FCSTD DOCUMENT  (FreeCAD 0.21R32532 (Git))
Label: 0
License: All rights reserved
LicenseURL: http://en.wikipedia.org/wiki/All_rights_reserved
objects: Part::Feature×1, Part::FeaturePython×1, Sketcher::SketchObject×1, PartDesign::SubShapeBinder×1
note: 4 computed .brp shape members not serialized (recipe doc carries the construction recipe); baked Part::Feature solids carry a one-line shape summary decoded from their .brp

FEATURE [Part::Feature] UNFOLD_SKETCH001
  shape: bbox 42770 x 1905 x 2e-07 mm, 0 faces, 0 solids (baked)
FEATURE [Part::FeaturePython] Clone  label="UNFOLD_SKETCH002"  # Draft clone (typed FeaturePython)
  AttacherType = Attacher::AttachEngine3D
  Fuse = false
  Objects = -> [UNFOLD_SKETCH001]
  Scale = (0.0393701,0.0393701,0.0393701)
  expr: .Scale.x = 1 / 25.4
  expr: .Scale.y = 1 / 25.4
  expr: .Scale.z = 1 / 25.4
FEATURE [Sketcher::SketchObject] Sketch
  FullyConstrained = true
  sketch-geometry (39):
    g0: Circle CenterX=1673 CenterY=0 CenterZ=0 NormalX=0 NormalY=0 NormalZ=1 AngleXU=0 Radius=1.7
    g1: Circle CenterX=1605 CenterY=-12.5 CenterZ=0 NormalX=0 NormalY=0 NormalZ=1 AngleXU=0 Radius=1.7
    g2: Circle CenterX=1605 CenterY=12.5 CenterZ=0 NormalX=0 NormalY=0 NormalZ=1 AngleXU=0 Radius=1.7
    g3: Circle CenterX=1584 CenterY=26.6981 CenterZ=0 NormalX=0 NormalY=0 NormalZ=1 AngleXU=0 Radius=1.7
    g4: Circle CenterX=1584 CenterY=0 CenterZ=0 NormalX=0 NormalY=0 NormalZ=1 AngleXU=0 Radius=1.7
    g5: Circle CenterX=1584 CenterY=-26.6981 CenterZ=0 NormalX=0 NormalY=0 NormalZ=1 AngleXU=0 Radius=1.7
    g6: Circle CenterX=1310.75 CenterY=-26.6981 CenterZ=0 NormalX=0 NormalY=0 NormalZ=1 AngleXU=0 Radius=1.7
    g7: Circle CenterX=1310.75 CenterY=0 CenterZ=0 NormalX=0 NormalY=0 NormalZ=1 AngleXU=0 Radius=1.7
    g8: Circle CenterX=1310.75 CenterY=26.6981 CenterZ=0 NormalX=0 NormalY=0 NormalZ=1 AngleXU=0 Radius=1.7
    g9: Circle CenterX=1037.5 CenterY=-26.6981 CenterZ=0 NormalX=0 NormalY=0 NormalZ=1 AngleXU=0 Radius=1.7
    g10: Circle CenterX=1037.5 CenterY=0 CenterZ=0 NormalX=0 NormalY=0 NormalZ=1 AngleXU=0 Radius=1.7
    g11: Circle CenterX=1037.5 CenterY=26.6981 CenterZ=0 NormalX=0 NormalY=0 NormalZ=1 AngleXU=0 Radius=1.7
    g12: Circle CenterX=764.248 CenterY=26.6981 CenterZ=0 NormalX=0 NormalY=0 NormalZ=1 AngleXU=0 Radius=1.7
    g13: Circle CenterX=764.248 CenterY=0 CenterZ=0 NormalX=0 NormalY=0 NormalZ=1 AngleXU=0 Radius=1.7
    g14: Circle CenterX=764.248 CenterY=-26.6981 CenterZ=0 NormalX=0 NormalY=0 NormalZ=1 AngleXU=0 Radius=1.7
    g15: Circle CenterX=490.999 CenterY=-26.6981 CenterZ=0 NormalX=0 NormalY=0 NormalZ=1 AngleXU=0 Radius=1.7
    g16: Circle CenterX=490.999 CenterY=0 CenterZ=0 NormalX=0 NormalY=0 NormalZ=1 AngleXU=0 Radius=1.7
    g17: Circle CenterX=469.999 CenterY=0 CenterZ=0 NormalX=0 NormalY=0 NormalZ=1 AngleXU=0 Radius=1.7
    g18: Circle CenterX=490.999 CenterY=26.6981 CenterZ=0 NormalX=0 NormalY=0 NormalZ=1 AngleXU=0 Radius=1.7
    g19: Circle CenterX=99.9998 CenterY=-26.1981 CenterZ=0 NormalX=0 NormalY=0 NormalZ=1 AngleXU=0 Radius=1.7
    g20: Circle CenterX=99.9998 CenterY=26.1981 CenterZ=0 NormalX=0 NormalY=0 NormalZ=1 AngleXU=0 Radius=1.7
    g21: Circle CenterX=71.3332 CenterY=26.1981 CenterZ=0 NormalX=0 NormalY=0 NormalZ=1 AngleXU=0 Radius=1.7
    g22: Circle CenterX=42.6666 CenterY=26.1981 CenterZ=0 NormalX=0 NormalY=0 NormalZ=1 AngleXU=0 Radius=1.7
    g23: Circle CenterX=14 CenterY=26.1981 CenterZ=0 NormalX=0 NormalY=0 NormalZ=1 AngleXU=0 Radius=1.7
    g24: Circle CenterX=14 CenterY=-26.1981 CenterZ=0 NormalX=0 NormalY=0 NormalZ=1 AngleXU=0 Radius=1.7
    g25: Circle CenterX=42.6666 CenterY=-26.1981 CenterZ=0 NormalX=0 NormalY=0 NormalZ=1 AngleXU=0 Radius=1.7
    g26: Circle CenterX=71.3332 CenterY=-26.1981 CenterZ=0 NormalX=0 NormalY=0 NormalZ=1 AngleXU=0 Radius=1.7
    g27: LineSegment StartX=0 StartY=-33.8132 StartZ=0 EndX=0 EndY=33.8132 EndZ=0
    g28: LineSegment StartX=0 StartY=33.8132 StartZ=0 EndX=1594 EndY=33.8132 EndZ=0
    g29: LineSegment StartX=1594 StartY=33.8132 StartZ=0 EndX=1594 EndY=14.3 EndZ=0
    g30: LineSegment StartX=1594 StartY=14.3 StartZ=0 EndX=1596 EndY=14.3 EndZ=0
    g31: LineSegment StartX=1596 StartY=14.3 StartZ=0 EndX=1596 EndY=37.5 EndZ=0
    g32: LineSegment StartX=1596 StartY=37.5 StartZ=0 EndX=1684 EndY=37.5 EndZ=0
    g33: LineSegment StartX=1684 StartY=37.5 StartZ=0 EndX=1684 EndY=-37.5 EndZ=0
    g34: LineSegment StartX=1684 StartY=-37.5 StartZ=0 EndX=1596 EndY=-37.5 EndZ=0
    g35: LineSegment StartX=1596 StartY=-37.5 StartZ=0 EndX=1596 EndY=-14.3 EndZ=0
    g36: LineSegment StartX=1596 StartY=-14.3 StartZ=0 EndX=1594 EndY=-14.3 EndZ=0
    g37: LineSegment StartX=1594 StartY=-14.3 StartZ=0 EndX=1594 EndY=-33.8132 EndZ=0
    g38: LineSegment StartX=1594 StartY=-33.8132 StartZ=0 EndX=0 EndY=-33.8132 EndZ=0
  constraints (62):
    c: Equal(g0, g1-g26) x26
    c: Diameter(g0) = 3.4
    c: Block(g0)
    c: Block(g1)
    c: Block(g2)
    c: Block(g3)
    c: Block(g4)
    c: Block(g5)
    c: Block(g6)
    c: Block(g7)
    c: Block(g8)
    c: Block(g9)
    c: Block(g10)
    c: Block(g11)
    c: Block(g12)
    c: Block(g13)
    c: Block(g14)
    c: Block(g15)
    c: Block(g16)
    c: Block(g17)
    c: Block(g18)
    c: Block(g19)
    c: Block(g20)
    c: Block(g21)
    c: Block(g22)
    c: Block(g23)
    c: Block(g24)
    c: Block(g25)
    c: Block(g26)
    c: PointOnObject(g27,g-2)
    c: Coincident(g27,g28)
    c: Horizontal(g28)
    c: Coincident(g28,g29)
    c: Vertical(g29)
    c: Coincident(g29,g30)
    c: Horizontal(g30)
    c: Coincident(g30,g31)
    c: Vertical(g31)
    c: Coincident(g31,g32)
    c: Horizontal(g32)
    c: Coincident(g32,g33)
    c: Vertical(g33)
    c: Coincident(g33,g34)
    c: Horizontal(g34)
    c: Coincident(g34,g35)
    c: Vertical(g35)
    c: Coincident(g35,g36)
    c: Coincident(g36,g37)
    c: Vertical(g37)
    c: Coincident(g37,g38)
    c: Coincident(g38,g27)
    c: Horizontal(g38)
    c: Symmetric(g27,g27,g-1)
    c: DistanceY(g27,g27) = 67.6264
    c: DistanceX(g28) = 1594
    c: DistanceX(g30,g30) = 2
    c: Horizontal(g36)
    c: Symmetric(g36,g29,g-1)
    c: DistanceY(g36,g29) = 28.6
    c: Symmetric(g31,g34,g-1)
    c: DistanceY(g31) = 37.5
    c: DistanceX(g32,g32) = 88
FEATURE [PartDesign::SubShapeBinder] Binder
  BindCopyOnChange = 0
  BindMode = 0
  ClaimChildren = false
  Fuse = false
  MakeFace = true
  OffsetFill = false
  OffsetIntersection = false
  OffsetJoinType = 0
  OffsetOpenResult = false
  PartialLoad = false
  Relative = true
  Support = -> [Clone[Edge1]]
  _Version = 2
